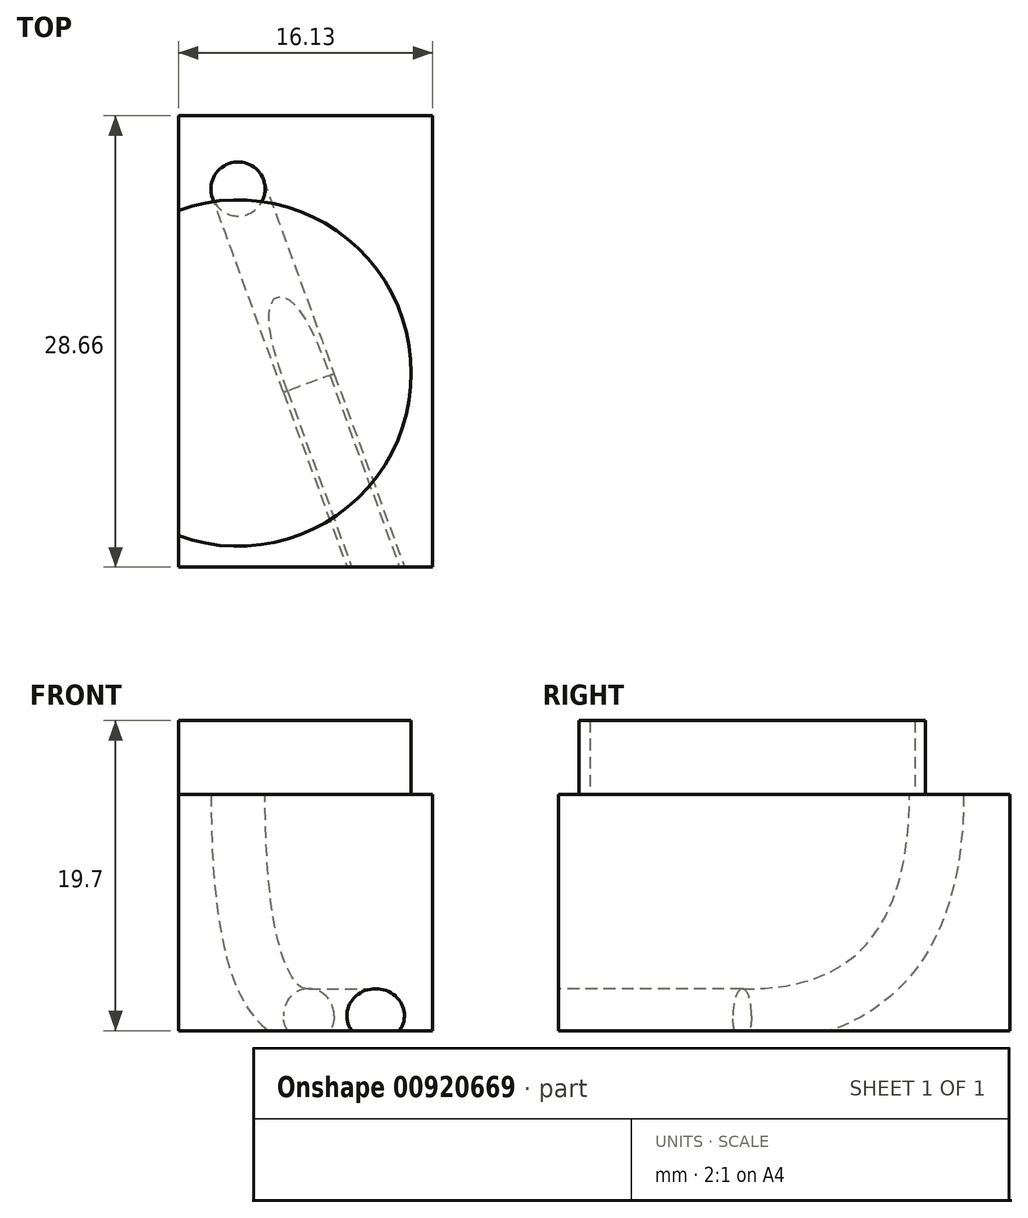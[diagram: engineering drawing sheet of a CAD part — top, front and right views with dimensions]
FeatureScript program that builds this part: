
annotation { "Feature Type Name" : "Feature", "Feature Type Description" : "" }
export const myFeature = defineFeature(function(context is Context, id is Id, definition is map)
    precondition{}
    {
        {
            var Q0;
            Q0=qCreatedBy(makeId("Top.planeOp"),FACE);
            var sketch = newSketch(context, id + "F0", { "sketchPlane" : qUnion([Q0])});
            skFitSpline(sketch, "E0", {"points": [v(0, 28) * mm, v(10.21, 28) * mm, v(22.09, 27.85) * mm, v(26.04, 25.64) * mm]});
            skFitSpline(sketch, "E1", {"points": [v(26.04, 25.64) * mm, v(28.02, 24.53) * mm, v(31.86, 21.89) * mm, v(33.37, 16.37) * mm]});
            skFitSpline(sketch, "E2", {"points": [v(33.37, 16.37) * mm, v(34.84, 11.02) * mm, v(34.65, -4.94) * mm, v(34.64, -5.79) * mm, v(34.64, -5.79) * mm, v(34.64, -5.8) * mm]});
            skFitSpline(sketch, "E3", {"points": [v(34.64, -5.8) * mm, v(34.64, -5.8) * mm, v(34.64, -5.8) * mm, v(34.87, -6.01) * mm, v(36.98, -7.98) * mm, v(36.83, -9.42) * mm]});
            skFitSpline(sketch, "E4", {"points": [v(36.83, -9.42) * mm, v(36.69, -10.77) * mm, v(35.78, -11.87) * mm, v(35.57, -12.1) * mm, v(35.57, -12.1) * mm, v(35.56, -12.12) * mm]});
            skFitSpline(sketch, "E5", {"points": [v(35.56, -12.12) * mm, v(35.55, -12.12) * mm, v(35.55, -12.12) * mm, v(35.3, -12.12) * mm, v(34.32, -12.12) * mm, v(34.07, -12.12) * mm, v(34.07, -12.12) * mm, v(34.05, -12.12) * mm]});
            skFitSpline(sketch, "E6", {"points": [v(34.05, -12.12) * mm, v(34.05, -12.13) * mm, v(34.05, -12.13) * mm, v(34.05, -13.28) * mm, v(34.05, -34.22) * mm, v(34.05, -35.36) * mm, v(34.05, -35.36) * mm, v(34.05, -35.38) * mm]});
            skFitSpline(sketch, "E7", {"points": [v(34.05, -35.38) * mm, v(34.07, -35.38) * mm, v(34.07, -35.38) * mm, v(34.33, -35.38) * mm, v(35.37, -35.38) * mm, v(35.63, -35.38) * mm, v(35.63, -35.38) * mm, v(35.65, -35.38) * mm]});
            skFitSpline(sketch, "E8", {"points": [v(35.65, -35.38) * mm, v(35.65, -35.38) * mm, v(35.65, -35.38) * mm, v(35.8, -35.53) * mm, v(37.06, -36.87) * mm, v(36.32, -37.9) * mm]});
            skFitSpline(sketch, "E9", {"points": [v(36.32, -37.9) * mm, v(35.53, -39.02) * mm, v(34.12, -39.7) * mm, v(32.87, -40.94) * mm]});
            skFitSpline(sketch, "E10", {"points": [v(32.87, -40.94) * mm, v(31.61, -42.17) * mm, v(27.4, -50.08) * mm, v(20.73, -54.34) * mm]});
            skFitSpline(sketch, "E11", {"points": [v(20.73, -54.34) * mm, v(14.06, -58.6) * mm, v(8.47, -61) * mm, v(0, -61) * mm, v(-8.46, -61) * mm, v(-14.06, -58.6) * mm, v(-20.73, -54.34) * mm]});
            skFitSpline(sketch, "E12", {"points": [v(-20.73, -54.34) * mm, v(-27.4, -50.08) * mm, v(-31.61, -42.17) * mm, v(-32.87, -40.94) * mm, v(-34.12, -39.7) * mm, v(-35.53, -39.02) * mm, v(-36.32, -37.9) * mm]});
            skFitSpline(sketch, "E13", {"points": [v(-36.32, -37.9) * mm, v(-37.06, -36.87) * mm, v(-35.8, -35.53) * mm, v(-35.65, -35.38) * mm, v(-35.65, -35.38) * mm, v(-35.65, -35.38) * mm]});
            skFitSpline(sketch, "E14", {"points": [v(-35.65, -35.38) * mm, v(-35.63, -35.38) * mm, v(-35.63, -35.38) * mm, v(-35.37, -35.38) * mm, v(-34.32, -35.38) * mm, v(-34.06, -35.38) * mm, v(-34.06, -35.38) * mm, v(-34.05, -35.38) * mm]});
            skFitSpline(sketch, "E15", {"points": [v(-34.05, -35.38) * mm, v(-34.05, -35.36) * mm, v(-34.05, -35.36) * mm, v(-34.05, -34.22) * mm, v(-34.05, -13.28) * mm, v(-34.05, -12.13) * mm, v(-34.05, -12.13) * mm, v(-34.05, -12.12) * mm]});
            skFitSpline(sketch, "E16", {"points": [v(-34.05, -12.12) * mm, v(-34.06, -12.12) * mm, v(-34.06, -12.12) * mm, v(-34.31, -12.12) * mm, v(-35.3, -12.12) * mm, v(-35.55, -12.12) * mm, v(-35.55, -12.12) * mm, v(-35.56, -12.12) * mm]});
            skFitSpline(sketch, "E17", {"points": [v(-35.56, -12.12) * mm, v(-35.57, -12.1) * mm, v(-35.57, -12.1) * mm, v(-35.78, -11.87) * mm, v(-36.69, -10.77) * mm, v(-36.83, -9.42) * mm, v(-36.98, -7.98) * mm, v(-34.87, -6.01) * mm, v(-34.64, -5.8) * mm, v(-34.64, -5.8) * mm, v(-34.64, -5.8) * mm]});
            skFitSpline(sketch, "E18", {"points": [v(-34.64, -5.8) * mm, v(-34.64, -5.79) * mm, v(-34.64, -5.79) * mm, v(-34.65, -4.94) * mm, v(-34.84, 11.02) * mm, v(-33.37, 16.37) * mm]});
            skFitSpline(sketch, "E19", {"points": [v(-33.37, 16.37) * mm, v(-31.85, 21.89) * mm, v(-28.02, 24.53) * mm, v(-26.04, 25.64) * mm, v(-22.09, 27.85) * mm, v(-10.2, 28) * mm, v(0, 28) * mm]});
            skLineSegment(sketch, "E20", {"start": v(-27.98, 0) * mm, "end": v(27.98, 0) * mm, "construction": true});
            skPoint(sketch, "E21", {"position": v(29.22, 0) * mm});
            skPoint(sketch, "E22.MirrorP", {"position": v(-29.22, 0) * mm});
            skCircle(sketch, "E23", {"center": v(0, -32) * mm, "radius": 11 * mm});
            skPoint(sketch, "E24", {"position": v(-15.59, -50.3) * mm});
            skPoint(sketch, "E25.MirrorP", {"position": v(15.59, -50.3) * mm});
            skPoint(sketch, "E26", {"position": v(0, 19.9) * mm});
            skSolve(sketch);
        }
        {
            var Q0;
            Q0=makeQuery(id+"F0.imprint","IMPRINT",FACE,{"disambiguationData":[TD([[makeQuery(id+"F0.imprint","IMPRINT",EDGE,{"derivedFrom":sQuery(id+"F0.wireOp",EDGE,"E23")}),1.0]])]});
            extrude(context, id + "F1", {"entities" : qUnion([Q0]), "depth" : 46 * mm, "offsetDistance" : 25 * mm});
        }
        {
            var Q0;
            Q0=makeQuery(id+"F0.imprint","IMPRINT",FACE,{"disambiguationData":[TD([[makeQuery(id+"F0.imprint","IMPRINT",EDGE,{"derivedFrom":sQuery(id+"F0.wireOp",EDGE,"E23")}),1.0]])]});
            var Q1;
            {var subQ1=sQuery(id+"F0.wireOp",EDGE,"E0");Q1=makeQuery(id+"F0.imprint","IMPRINT",FACE,{"disambiguationData":[TD([[makeQuery(id+"F0.imprint","IMPRINT",EDGE,{"derivedFrom":subQ1}),-1.0]])]});}
            extrude(context, id + "F2", {"entities" : qUnion([Q0, Q1]), "operationType" : NewBodyOperationType.ADD, "oppositeDirection" : true, "depth" : 12 * mm, "offsetDistance" : 25 * mm});
        }
        {
            var Q0;
            Q0=sQuery(id+"F0.wireOp",VERTEX,"E25.MirrorP");
            var Q1;
            Q1=sQuery(id+"F0.wireOp",VERTEX,"E24");
            var Q2;
            Q2=makeQuery(id+"F1.opExtrude","SWEPT_BODY",BODY,{"disambiguationData":[OSD([sQuery(id+"F0.wireOp",EDGE,"E23")])]});
            hole(context, id + "F3", {"style" : HoleStyle.C_BORE, "endStyle" : HoleEndStyle.THROUGH, "holeDiameter" : 9 * mm, "cBoreDiameter" : 12 * mm, "cBoreDepth" : 3 * mm, "majorDiameter" : 5 * mm, "isTappedThrough" : true, "tappedDepth" : 12 * mm, "tapClearance" : 3, "locations" : qUnion([Q0, Q1]), "scope" : qUnion([Q2])});
        }
        {
            var Q0;
            Q0=sQuery(id+"F0.wireOp",VERTEX,"E26");
            var Q1;
            Q1=makeQuery(id+"F1.opExtrude","SWEPT_BODY",BODY,{"disambiguationData":[OSD([sQuery(id+"F0.wireOp",EDGE,"E23")])]});
            hole(context, id + "F4", {"style" : HoleStyle.C_BORE, "endStyle" : HoleEndStyle.BLIND, "holeDiameter" : 9 * mm, "cBoreDiameter" : 17 * mm, "cBoreDepth" : 3 * mm, "majorDiameter" : 5 * mm, "holeDepth" : 12 * mm, "isTappedThrough" : true, "tappedDepth" : 12 * mm, "tapClearance" : 3, "locations" : qUnion([Q0]), "scope" : qUnion([Q1])});
        }
        {
            var Q0;
            Q0=sQuery(id+"F0.wireOp",VERTEX,"E22.MirrorP");
            var Q1;
            Q1=sQuery(id+"F0.wireOp",VERTEX,"E21");
            var Q2;
            Q2=makeQuery(id+"F1.opExtrude","SWEPT_BODY",BODY,{"disambiguationData":[OSD([sQuery(id+"F0.wireOp",EDGE,"E23")])]});
            hole(context, id + "F5", {"style" : HoleStyle.C_BORE, "endStyle" : HoleEndStyle.THROUGH, "holeDiameter" : 3 * mm, "cBoreDiameter" : 6 * mm, "cBoreDepth" : 10 * mm, "majorDiameter" : 5 * mm, "isTappedThrough" : true, "tappedDepth" : 12 * mm, "tapClearance" : 3, "locations" : qUnion([Q0, Q1]), "scope" : qUnion([Q2])});
        }
        {
            var Q0;
            Q0=makeQuery(id+"F2.opExtrude","CAP_FACE",FACE,{"disambiguationData":[OSD([sQuery(id+"F0.wireOp",EDGE,"E0"),sQuery(id+"F0.wireOp",EDGE,"E1"),sQuery(id+"F0.wireOp",EDGE,"E2"),sQuery(id+"F0.wireOp",EDGE,"E3"),sQuery(id+"F0.wireOp",EDGE,"E4"),sQuery(id+"F0.wireOp",EDGE,"E5"),sQuery(id+"F0.wireOp",EDGE,"E6"),sQuery(id+"F0.wireOp",EDGE,"E7"),sQuery(id+"F0.wireOp",EDGE,"E8"),sQuery(id+"F0.wireOp",EDGE,"E9"),sQuery(id+"F0.wireOp",EDGE,"E10"),sQuery(id+"F0.wireOp",EDGE,"E11"),sQuery(id+"F0.wireOp",EDGE,"E12"),sQuery(id+"F0.wireOp",EDGE,"E12"),sQuery(id+"F0.wireOp",EDGE,"E13"),sQuery(id+"F0.wireOp",EDGE,"E14"),sQuery(id+"F0.wireOp",EDGE,"E15"),sQuery(id+"F0.wireOp",EDGE,"E16"),sQuery(id+"F0.wireOp",EDGE,"E17"),sQuery(id+"F0.wireOp",EDGE,"E17"),sQuery(id+"F0.wireOp",EDGE,"E18"),sQuery(id+"F0.wireOp",EDGE,"E19"),sQuery(id+"F0.wireOp",EDGE,"E19")])],"isStart":false});
            var sketch = newSketch(context, id + "F6", { "sketchPlane" : qUnion([Q0])});
            skLineSegment(sketch, "E27.bottom", {"start": v(-43, -32.02) * mm, "end": v(43, -32.02) * mm});
            skLineSegment(sketch, "E27.top", {"start": v(-43, 63.98) * mm, "end": v(43, 63.98) * mm});
            skLineSegment(sketch, "E27.left", {"start": v(-43, -32.02) * mm, "end": v(-43, 63.98) * mm});
            skLineSegment(sketch, "E27.right", {"start": v(43, -32.02) * mm, "end": v(43, 63.98) * mm});
            skPoint(sketch, "E28", {"position": v(0, 63.98) * mm});
            skSolve(sketch);
        }
        {
            var Q0;
            Q0 = qSketchRegion(id + "F6", true);
            extrude(context, id + "F7", {"entities" : qUnion([Q0]), "operationType" : NewBodyOperationType.ADD, "depth" : 3 * mm, "offsetDistance" : 25 * mm});
        }
        {
            var Q0;
            Q0=qCreatedBy(makeId("Front.planeOp"),FACE);
            var sketch = newSketch(context, id + "F8", { "sketchPlane" : qUnion([Q0])});
            skLineSegment(sketch, "E29.bottom", {"start": v(43, -12) * mm, "end": v(44.94, -12) * mm});
            skLineSegment(sketch, "E29.top", {"start": v(43, -18.74) * mm, "end": v(44.94, -18.74) * mm});
            skLineSegment(sketch, "E29.left", {"start": v(43, -12) * mm, "end": v(43, -18.74) * mm});
            skLineSegment(sketch, "E29.right", {"start": v(44.94, -12) * mm, "end": v(44.94, -18.74) * mm});
            skPoint(sketch, "E30", {"position": v(43, -12) * mm});
            skLineSegment(sketch, "E31.bottom", {"start": v(43, -18.74) * mm, "end": v(40.97, -18.74) * mm});
            skLineSegment(sketch, "E31.top", {"start": v(43, -17.05) * mm, "end": v(40.97, -17.05) * mm});
            skLineSegment(sketch, "E31.left", {"start": v(43, -18.74) * mm, "end": v(43, -17.05) * mm});
            skLineSegment(sketch, "E31.right", {"start": v(40.97, -18.74) * mm, "end": v(40.97, -17.05) * mm});
            skSolve(sketch);
        }
        {
            var Q0;
            {var subQ0=sQuery(id+"F8.wireOp",EDGE,"E31.bottom");var subQ6=sQuery(id+"F8.wireOp",EDGE,"E29.bottom");Q0=qUnion([makeQuery(id+"F8.imprint","IMPRINT",FACE,{"disambiguationData":[TD([[makeQuery(id+"F8.imprint","IMPRINT",EDGE,{"derivedFrom":subQ6}),-1.0]])]}),makeQuery(id+"F8.imprint","IMPRINT",FACE,{"disambiguationData":[TD([[makeQuery(id+"F8.imprint","IMPRINT",EDGE,{"derivedFrom":subQ0}),-1.0]])]})]);}
            var Q1;
            Q1=makeQuery(id+"F7.opExtrude","CAP_EDGE",EDGE,{"disambiguationData":[OSD([sQuery(id+"F6.wireOp",EDGE,"E27.right")])],"isStart":false});
            var Q2;
            Q2=makeQuery(id+"F7.opExtrude","CAP_EDGE",EDGE,{"disambiguationData":[OSD([sQuery(id+"F6.wireOp",EDGE,"E27.top")])],"isStart":false});
            var Q3;
            Q3=makeQuery(id+"F7.opExtrude","CAP_EDGE",EDGE,{"disambiguationData":[OSD([sQuery(id+"F6.wireOp",EDGE,"E27.left")])],"isStart":false});
            sweep(context, id + "F9", {"operationType" : NewBodyOperationType.ADD, "profiles" : qUnion([Q0]), "path" : qUnion([Q1, Q2, Q3])});
        }
        {
            var Q0;
            Q0=makeQuery(id+"F9.opSweep","MID_CAP_EDGE",EDGE,{"disambiguationData":[OSD([sQuery(id+"F6.wireOp",EDGE,"E27.top"),sQuery(id+"F6.wireOp",EDGE,"E27.right"),sQuery(id+"F8.wireOp",EDGE,"E29.right")])],"capPos":1.0});
            var Q1;
            Q1=makeQuery(id+"F9.opSweep","MID_CAP_EDGE",EDGE,{"disambiguationData":[OSD([sQuery(id+"F6.wireOp",EDGE,"E27.top"),sQuery(id+"F6.wireOp",EDGE,"E27.left"),sQuery(id+"F8.wireOp",EDGE,"E29.right")])],"capPos":2.0});
            fillet(context, id + "F10", {"entities" : qUnion([Q0, Q1]), "tangentPropagation" : true, "radius" : 6 * mm, "defaultsChanged" : false, "vertexSettings" : [], "allowEdgeOverflow" : false});
        }
        {
            var Q0;
            Q0=makeQuery(id+"F9.opSweep","MID_CAP_EDGE",EDGE,{"disambiguationData":[OSD([sQuery(id+"F6.wireOp",EDGE,"E27.top"),sQuery(id+"F6.wireOp",EDGE,"E27.left"),sQuery(id+"F8.wireOp",EDGE,"E31.right")])],"capPos":2.0});
            var Q1;
            Q1=makeQuery(id+"F9.opSweep","MID_CAP_EDGE",EDGE,{"disambiguationData":[OSD([sQuery(id+"F6.wireOp",EDGE,"E27.top"),sQuery(id+"F6.wireOp",EDGE,"E27.right"),sQuery(id+"F8.wireOp",EDGE,"E31.right")])],"capPos":1.0});
            fillet(context, id + "F11", {"entities" : qUnion([Q0, Q1]), "tangentPropagation" : true, "radius" : 5 * mm, "defaultsChanged" : false, "vertexSettings" : [], "allowEdgeOverflow" : false});
        }
        {
            var Q0;
            Q0=qCreatedBy(makeId("Right.planeOp"),FACE);
            var sketch = newSketch(context, id + "F12", { "sketchPlane" : qUnion([Q0])});
            skLineSegment(sketch, "E32", {"start": v(-20.3, 0) * mm, "end": v(-20.3, 23.52) * mm});
            skSolve(sketch);
        }
        {
            var Q0;
            Q0=sQuery(id+"F14.wireOp",EDGE,"E35");
            var Q1;
            Q1=sQuery(id+"F12.wireOp",EDGE,"E32");
            cPlane(context, id + "F13", {"entities" : qUnion([Q0, Q1]), "cplaneType" : CPlaneType.LINE_ANGLE, "offset" : 25 * mm, "angle" : 20 * degree, "width" : 150 * mm, "height" : 150 * mm});
        }
        {
            var Q0;
            Q0=qCreatedBy(id+"F13.planeOp",FACE);
            var sketch = newSketch(context, id + "F14", { "sketchPlane" : qUnion([Q0])});
            skFitSpline(sketch, "E33", {"points": [v(-19.08, 0) * mm, v(-32.22, -14.05) * mm], "startDerivative": vector(0, -26.3) * mm, "endDerivative": vector(-27.68, 0.48) * mm});
            skLineSegment(sketch, "E34", {"start": v(-32.22, -14.05) * mm, "end": v(-47.22, -14.05) * mm});
            skLineSegment(sketch, "E35", {"start": v(-19.08, 0) * mm, "end": v(-19.08, 23.52) * mm});
            skSolve(sketch);
        }
        {
            var Q0;
            Q0=sQuery(id+"F0.wireOp",VERTEX,"E26");
            var Q1;
            Q1=sQuery(id+"F0.wireOp",VERTEX,"E24");
            var Q2;
            Q2=sQuery(id+"F0.wireOp",VERTEX,"E25.MirrorP");
            var Q3;
            Q3=makeQuery(id+"F1.opExtrude","SWEPT_BODY",BODY,{"disambiguationData":[OSD([sQuery(id+"F0.wireOp",EDGE,"E23")])]});
            hole(context, id + "F15", {"style" : HoleStyle.SIMPLE, "endStyle" : HoleEndStyle.THROUGH, "holeDiameter" : 2 * mm, "majorDiameter" : 5 * mm, "isTappedThrough" : true, "tappedDepth" : 12 * mm, "tapClearance" : 3, "locations" : qUnion([Q0, Q1, Q2]), "scope" : qUnion([Q3])});
        }
        {
            var Q0;
            Q0=sQuery(id+"F0.wireOp",VERTEX,"E22.MirrorP");
            var Q1;
            Q1=sQuery(id+"F0.wireOp",VERTEX,"E21");
            var Q2;
            Q2=makeQuery(id+"F1.opExtrude","SWEPT_BODY",BODY,{"disambiguationData":[OSD([sQuery(id+"F0.wireOp",EDGE,"E23")])]});
            hole(context, id + "F16", {"style" : HoleStyle.SIMPLE, "endStyle" : HoleEndStyle.THROUGH, "holeDiameter" : 4 * mm, "majorDiameter" : 5 * mm, "isTappedThrough" : true, "tappedDepth" : 12 * mm, "tapClearance" : 3, "locations" : qUnion([Q0, Q1]), "scope" : qUnion([Q2])});
        }
        {
            var Q0;
            Q0=qCreatedBy(makeId("Top.planeOp"),FACE);
            var sketch = newSketch(context, id + "F17", { "sketchPlane" : qUnion([Q0])});
            skCircle(sketch, "E36", {"center": v(0, -20.3) * mm, "radius": 1.72 * mm});
            skSolve(sketch);
        }
        {
            var Q0;
            Q0=makeQuery(id+"F17.imprint","IMPRINT",FACE,{"disambiguationData":[TD([[makeQuery(id+"F17.imprint","IMPRINT",EDGE,{"derivedFrom":sQuery(id+"F17.wireOp",EDGE,"E36")}),1.0]])]});
            var Q1;
            Q1=sQuery(id+"F14.wireOp",EDGE,"E33");
            var Q2;
            Q2=sQuery(id+"F14.wireOp",EDGE,"E34");
            sweep(context, id + "F18", {"operationType" : NewBodyOperationType.REMOVE, "profiles" : qUnion([Q0]), "path" : qUnion([Q1, Q2])});
        }
        {
            var Q0;
            Q0=qCreatedBy(makeId("Right.planeOp"),FACE);
            cPlane(context, id + "F19", {"entities" : qUnion([Q0]), "cplaneType" : CPlaneType.OFFSET, "offset" : 9 * mm, "width" : 150 * mm, "height" : 150 * mm});
        }
        {
            var Q0;
            Q0=makeQuery(id+"F7.opExtrude","CAP_FACE",FACE,{"disambiguationData":[OSD([sQuery(id+"F6.wireOp",EDGE,"E27.bottom"),sQuery(id+"F6.wireOp",EDGE,"E27.top"),sQuery(id+"F6.wireOp",EDGE,"E27.left"),sQuery(id+"F6.wireOp",EDGE,"E27.right")])],"isStart":false});
            var sketch = newSketch(context, id + "F20", { "sketchPlane" : qUnion([Q0])});
            skLineSegment(sketch, "E37.bottom", {"start": v(-3.78, 44.32) * mm, "end": v(12.35, 44.32) * mm});
            skLineSegment(sketch, "E37.top", {"start": v(-3.78, 15.66) * mm, "end": v(12.35, 15.66) * mm});
            skLineSegment(sketch, "E37.left", {"start": v(-3.78, 44.32) * mm, "end": v(-3.78, 15.66) * mm});
            skLineSegment(sketch, "E37.right", {"start": v(12.35, 44.32) * mm, "end": v(12.35, 15.66) * mm});
            skSolve(sketch);
        }
        {
            var Q0;
            Q0 = qSketchRegion(id + "F20", true);
            extrude(context, id + "F21", {"entities" : qUnion([Q0]), "operationType" : NewBodyOperationType.INTERSECT, "oppositeDirection" : true, "depth" : 19.7 * mm, "offsetDistance" : 25 * mm});
        }
    });
